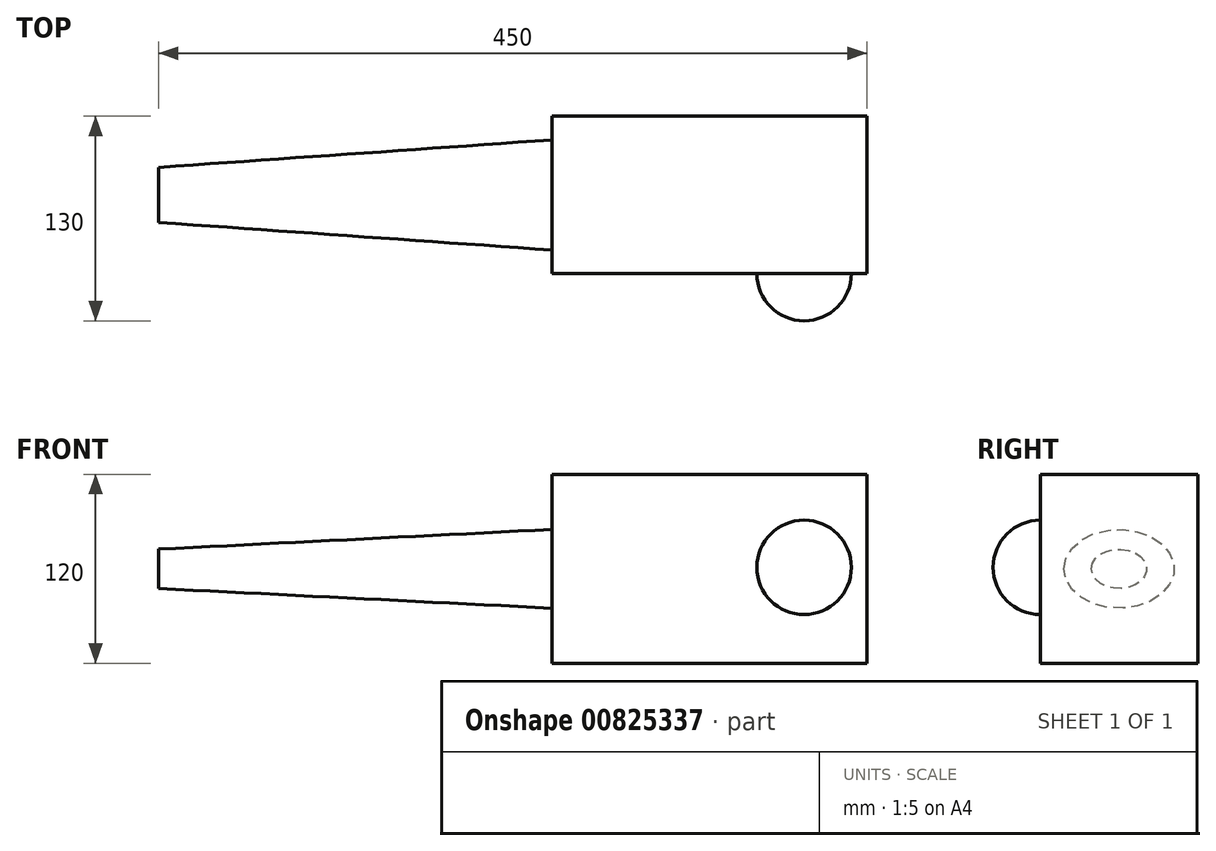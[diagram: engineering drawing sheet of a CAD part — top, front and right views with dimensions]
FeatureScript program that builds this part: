
annotation { "Feature Type Name" : "Feature", "Feature Type Description" : "" }
export const myFeature = defineFeature(function(context is Context, id is Id, definition is map)
    precondition{}
    {
        {
            var Q0;
            Q0=qCreatedBy(makeId("Top.planeOp"),FACE);
            var sketch = newSketch(context, id + "F0", { "sketchPlane" : qUnion([Q0])});
            skLineSegment(sketch, "E0.bottom", {"start": v(-2540, -1170) * mm, "end": v(-2340, -1170) * mm});
            skLineSegment(sketch, "E0.top", {"start": v(-2540, -1270) * mm, "end": v(-2340, -1270) * mm});
            skLineSegment(sketch, "E0.left", {"start": v(-2540, -1170) * mm, "end": v(-2540, -1270) * mm});
            skLineSegment(sketch, "E0.right", {"start": v(-2340, -1170) * mm, "end": v(-2340, -1270) * mm});
            skSolve(sketch);
        }
        {
            var Q0;
            Q0 = qSketchRegion(id + "F0", true);
            extrude(context, id + "F1", {"entities" : qUnion([Q0]), "depth" : 120 * mm, "offsetDistance" : 25.4 * mm});
        }
        {
            var Q0;
            Q0=makeQuery(id+"F1.opExtrude","SWEPT_FACE",FACE,{"disambiguationData":[OSD([sQuery(id+"F0.wireOp",EDGE,"E0.top")])]});
            var sketch = newSketch(context, id + "F2", { "sketchPlane" : qUnion([Q0])});
            skArc(sketch, "E1", {"start": v(-2380, 30.95) * mm, "mid": v(-2350, 60.95) * mm, "end": v(-2380, 90.95) * mm});
            skLineSegment(sketch, "E2", {"start": v(-2540, 60.95) * mm, "end": v(-2340, 60.95) * mm, "construction": true});
            skLineSegment(sketch, "E3", {"start": v(-2340, 60.95) * mm, "end": v(-2380, 60.95) * mm, "construction": true});
            skLineSegment(sketch, "E4", {"start": v(-2380, 90.95) * mm, "end": v(-2380, 30.95) * mm});
            skSolve(sketch);
        }
        {
            var Q0;
            Q0=makeQuery(id+"F2.imprint","IMPRINT",FACE,{"disambiguationData":[TD([[makeQuery(id+"F2.imprint","IMPRINT",EDGE,{"derivedFrom":sQuery(id+"F2.wireOp",EDGE,"E1")}),1.0]])]});
            var Q1;
            Q1=sQuery(id+"F2.wireOp",EDGE,"E4");
            revolve(context, id + "F3", {"operationType" : NewBodyOperationType.ADD, "surfaceOperationType" : NewSurfaceOperationType.NEW, "entities" : qUnion([Q0]), "axis" : qUnion([Q1]), "revolveType" : RevolveType.FULL});
        }
        {
            var Q0;
            Q0=makeQuery(id+"F1.opExtrude","SWEPT_FACE",FACE,{"disambiguationData":[OSD([sQuery(id+"F0.wireOp",EDGE,"E0.left")])]});
            var sketch = newSketch(context, id + "F4", { "sketchPlane" : qUnion([Q0])});
            skLineSegment(sketch, "E5", {"start": v(1170, 60) * mm, "end": v(1270, 60) * mm, "construction": true});
            skSolve(sketch);
        }
        {
            var Q0;
            {var subQ0=sQuery(id+"F0.wireOp",EDGE,"E0.left");Q0=makeQuery(id+"F4.imprint","IMPRINT",FACE,{"disambiguationData":[TD([[makeQuery(id+"F4.imprint","IMPRINT",EDGE,{"derivedFrom":makeQuery(id+"F1.opExtrude","CAP_EDGE",EDGE,{"disambiguationData":[OSD([subQ0])],"isStart":true})}),1.0]])]});}
            var sketch = newSketch(context, id + "F5", { "sketchPlane" : qUnion([Q0])});
            skEllipse(sketch, "E6", {"center": v(1220, 60) * mm, "majorRadius": 35 * mm, "minorRadius": 25 * mm, "majorAxis": v(1, 0)});
            skSolve(sketch);
        }
        {
            var Q0;
            {var subQ0=sQuery(id+"F0.wireOp",EDGE,"E0.left");Q0=makeQuery(id+"F4.imprint","IMPRINT",FACE,{"disambiguationData":[TD([[makeQuery(id+"F4.imprint","IMPRINT",EDGE,{"derivedFrom":makeQuery(id+"F1.opExtrude","CAP_EDGE",EDGE,{"disambiguationData":[OSD([subQ0])],"isStart":true})}),1.0]])]});}
            cPlane(context, id + "F6", {"entities" : qUnion([Q0]), "cplaneType" : CPlaneType.OFFSET, "offset" : 250 * mm, "width" : 150 * mm, "height" : 150 * mm});
        }
        {
            var Q0;
            Q0=qCreatedBy(id+"F6.planeOp",FACE);
            var sketch = newSketch(context, id + "F7", { "sketchPlane" : qUnion([Q0])});
            skEllipse(sketch, "E7", {"center": v(1220, 60) * mm, "majorRadius": 17.5 * mm, "minorRadius": 12.5 * mm, "majorAxis": v(1, 0)});
            skSolve(sketch);
        }
        {
            var Q1;
            Q1=makeQuery(id+"F5.imprint","IMPRINT",FACE,{"disambiguationData":[TD([[makeQuery(id+"F5.imprint","IMPRINT",EDGE,{"derivedFrom":sQuery(id+"F5.wireOp",EDGE,"E6")}),1.0]])]});
            var Q2;
            Q2=makeQuery(id+"F7.imprint","IMPRINT",FACE,{"disambiguationData":[TD([[makeQuery(id+"F7.imprint","IMPRINT",EDGE,{"derivedFrom":sQuery(id+"F7.wireOp",EDGE,"E7")}),1.0]])]});
            loft(context, id + "F8", {"operationType" : NewBodyOperationType.ADD, "sheetProfilesArray" : [{ "sheetProfileEntities" : qUnion([Q1]) }, { "sheetProfileEntities" : qUnion([Q2]) }]});
        }
    });
